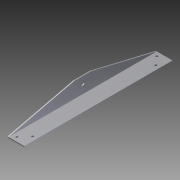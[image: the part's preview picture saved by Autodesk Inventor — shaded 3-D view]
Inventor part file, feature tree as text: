
AUTODESK INVENTOR PART (.ipt)
format: ipt  version: 2012 (Build 160160000, 160)  size: 109,568 bytes
history: native  units: in
note: dims shown in document units (in); Inventor stores cm internally (conversion verified against a paired STEP export)
features: extrude x3, sketch x3
ambient origin geometry x8: Origin, YZ Plane, XZ Plane, XY Plane, X Axis, Y Axis, Z Axis, Center Point
bodies: Solid1 (feature_tree)
feature tree (6):
  extrude  "Extrusion1"  Depth=0.0625in
  extrude  "Extrusion2"  Depth=1.0in
  extrude  "Extrusion3"  Depth=0.125in
  sketch  "Sketch1"  dims[d0=0.0625in d1=0.0625in]
  sketch  "Sketch2"  dims[d2=1.0in d3=1.0in]
  sketch  "Sketch3"  dims[d4=8.875in d5=0.0in d6=0.125in d7=0.25in d8=0.3125in d9=0.75in d10=0.25in d11=8.875in d12=0.0in d13=0.25in d14=0.625in d15=4.4375in d16=0.0625in d17=0.0625in d18=0.5in d19=1.0in d20=8.875in d21=0.0in]
